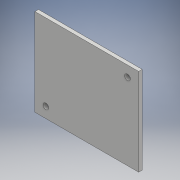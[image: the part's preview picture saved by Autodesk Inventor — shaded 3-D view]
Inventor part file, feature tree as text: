
AUTODESK INVENTOR PART (.ipt)
format: ipt  version: 2017 (Build 210142000, 142)  size: 157,696 bytes
history: native  units: mm
features: sketch x3, extrude x2, hole x1
ambient origin geometry x8: Origin, YZ Plane, XZ Plane, XY Plane, X Axis, Y Axis, Z Axis, Center Point
bodies: Solid1 (feature_tree)
feature tree (6):
  extrude  "Extrusion1"  Depth=61.3mm
  hole  "Hole1"  [1 undecoded]
  extrude  "Extrusion2"  Depth=7.5mm
  sketch  "Sketch1"  dims[d0=72.9mm d1=61.3mm]
  sketch  "Sketch2"  dims[d2=2.5mm d3=0.0mm d6=7.7mm]
  sketch  "Sketch3"  dims[d7=7.5mm d8=7.5mm d9=7.8mm d10=4.0mm d11=6.0mm d12=4.0mm d13=2.0mm d14=90.0deg d15=8.0mm d16=0.0mm d17=42.885722mm d18=15.0mm d19=16.691549mm d20=22.3mm d21=2.0mm d22=0.0mm]
note: 1 required parameter value undecoded (feature->parameter linkage not recoverable at this tier; creation-order binding heuristic only, values carry confidence <= 0.55)
